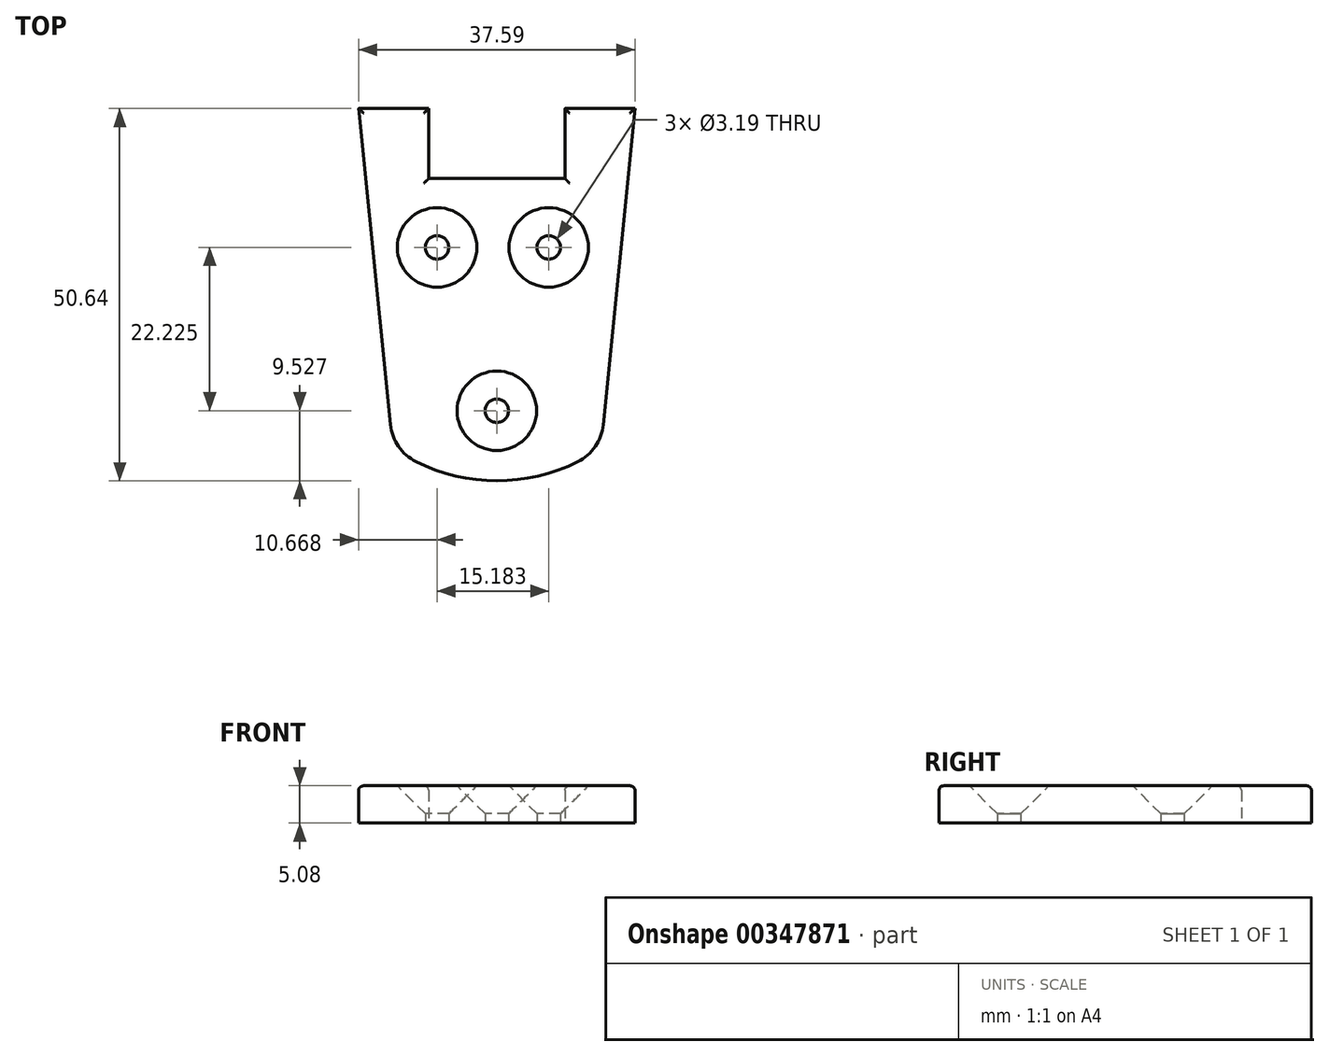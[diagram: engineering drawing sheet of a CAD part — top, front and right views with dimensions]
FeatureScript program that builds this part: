
annotation { "Feature Type Name" : "Feature", "Feature Type Description" : "" }
export const myFeature = defineFeature(function(context is Context, id is Id, definition is map)
    precondition{}
    {
        {
            var Q0;
            Q0=qCreatedBy(makeId("Top.planeOp"),FACE);
            var sketch = newSketch(context, id + "F0", { "sketchPlane" : qUnion([Q0])});
            skLineSegment(sketch, "E0", {"start": v(4.33, 7.8) * mm, "end": v(0, 50.8) * mm});
            skLineSegment(sketch, "E1", {"start": v(0, 50.8) * mm, "end": v(9.53, 50.8) * mm});
            skLineSegment(sketch, "E2", {"start": v(9.53, 50.8) * mm, "end": v(9.53, 41.28) * mm});
            skLineSegment(sketch, "E3", {"start": v(9.53, 41.28) * mm, "end": v(28.07, 41.28) * mm});
            skLineSegment(sketch, "E4", {"start": v(28.07, 41.28) * mm, "end": v(28.07, 50.8) * mm});
            skLineSegment(sketch, "E5", {"start": v(28.07, 50.8) * mm, "end": v(37.6, 50.8) * mm});
            skLineSegment(sketch, "E6", {"start": v(37.6, 50.8) * mm, "end": v(33.3, 7.8) * mm});
            skArc(sketch, "E7", {"start": v(7.8, 2.76) * mm, "mid": v(18.8, 0.16) * mm, "end": v(29.8, 2.75) * mm});
            skCircle(sketch, "E8", {"center": v(18.8, 9.69) * mm, "radius": 1.6 * mm});
            skCircle(sketch, "E9", {"center": v(25.85, 31.91) * mm, "radius": 1.6 * mm});
            skCircle(sketch, "E10", {"center": v(10.67, 31.91) * mm, "radius": 1.6 * mm});
            skPoint(sketch, "E11.visualSharp", {"position": v(32.98, 4.64) * mm});
            skArc(sketch, "E11.filletArc", {"start": v(29.8, 2.75) * mm, "mid": v(32.2, 4.83) * mm, "end": v(33.3, 7.8) * mm});
            skPoint(sketch, "E12.visualSharp", {"position": v(4.64, 4.65) * mm});
            skArc(sketch, "E12.filletArc", {"start": v(4.33, 7.8) * mm, "mid": v(5.42, 4.83) * mm, "end": v(7.8, 2.76) * mm});
            skSolve(sketch);
        }
        {
            var Q0;
            Q0=makeQuery(id+"F0.imprint","IMPRINT",FACE,{"disambiguationData":[TD([[makeQuery(id+"F0.imprint","IMPRINT",EDGE,{"derivedFrom":sQuery(id+"F0.wireOp",EDGE,"E0")}),-1.0]])]});
            extrude(context, id + "F1", {"entities" : qUnion([Q0]), "depth" : 5.08 * mm});
        }
        {
            var Q0;
            Q0=makeQuery(id+"F1.opExtrude","CAP_EDGE",EDGE,{"disambiguationData":[OSD([sQuery(id+"F0.wireOp",EDGE,"E10")])],"isStart":false});
            var Q1;
            Q1=makeQuery(id+"F1.opExtrude","CAP_EDGE",EDGE,{"disambiguationData":[OSD([sQuery(id+"F0.wireOp",EDGE,"E9")])],"isStart":false});
            var Q2;
            Q2=makeQuery(id+"F1.opExtrude","CAP_EDGE",EDGE,{"disambiguationData":[OSD([sQuery(id+"F0.wireOp",EDGE,"E8")])],"isStart":false});
            chamfer(context, id + "F2", {"entities" : qUnion([Q0, Q1, Q2]), "width" : 3.8 * mm, "tangentPropagation" : true});
        }
        {
            var Q0;
            Q0=makeQuery(id+"F1.opExtrude","CAP_EDGE",EDGE,{"disambiguationData":[OSD([sQuery(id+"F0.wireOp",EDGE,"E7")])],"isStart":false});
            var Q1;
            Q1=makeQuery(id+"F1.opExtrude","CAP_EDGE",EDGE,{"disambiguationData":[OSD([sQuery(id+"F0.wireOp",EDGE,"E11.filletArc")])],"isStart":false});
            var Q2;
            Q2=makeQuery(id+"F1.opExtrude","CAP_EDGE",EDGE,{"disambiguationData":[OSD([sQuery(id+"F0.wireOp",EDGE,"E5")])],"isStart":false});
            var Q3;
            Q3=makeQuery(id+"F1.opExtrude","CAP_EDGE",EDGE,{"disambiguationData":[OSD([sQuery(id+"F0.wireOp",EDGE,"E2")])],"isStart":false});
            var Q4;
            Q4=makeQuery(id+"F1.opExtrude","CAP_EDGE",EDGE,{"disambiguationData":[OSD([sQuery(id+"F0.wireOp",EDGE,"E6")])],"isStart":false});
            var Q5;
            Q5=makeQuery(id+"F1.opExtrude","CAP_EDGE",EDGE,{"disambiguationData":[OSD([sQuery(id+"F0.wireOp",EDGE,"E0")])],"isStart":false});
            var Q6;
            Q6=makeQuery(id+"F1.opExtrude","CAP_EDGE",EDGE,{"disambiguationData":[OSD([sQuery(id+"F0.wireOp",EDGE,"E1")])],"isStart":false});
            var Q7;
            Q7=makeQuery(id+"F1.opExtrude","CAP_EDGE",EDGE,{"disambiguationData":[OSD([sQuery(id+"F0.wireOp",EDGE,"E4")])],"isStart":false});
            var Q8;
            Q8=makeQuery(id+"F1.opExtrude","CAP_EDGE",EDGE,{"disambiguationData":[OSD([sQuery(id+"F0.wireOp",EDGE,"E12.filletArc")])],"isStart":false});
            var Q9;
            Q9=makeQuery(id+"F1.opExtrude","CAP_EDGE",EDGE,{"disambiguationData":[OSD([sQuery(id+"F0.wireOp",EDGE,"E3")])],"isStart":false});
            fillet(context, id + "F3", {"entities" : qUnion([Q0, Q1, Q2, Q3, Q4, Q5, Q6, Q7, Q8, Q9]), "radius" : 0.64 * mm, "tangentPropagation" : true, "allowEdgeOverflow" : false});
        }
    });
